# Revit family: Showerhead-American_Standard-FloWise-1660.613_Series
name_source: partatom
category: Plumbing Fixtures
units: mm (PartAtom-declared; Revit-internal decimal feet)

## family parameters
Always vertical = No
Cut with Voids When Loaded = No
OmniClass Number = 23.45.05.14.17
OmniClass Title = Showers
Part Type = Normal
Room Calculation Point = No
Round Connector Dimension = Use Diameter
Shared = Yes
Work Plane-Based = Yes

## types (1)
- 1660.613.002
    Assembly Code = D2010710
    CW Connection = No
    CWFU = 3
    Default Elevation = 0"
    Description = FloWise Modern 3-Function Water Saving Showerhead
    Finish = Brass-American Standard-002-Polished Chrome
    Flow Rate = 2.0 gpm Max Flow Rate
    HW Connection = No
    HWFU = 3
    Height = 4 3/4"
    Manufacturer = American Standard
    Material = Brass-American Standard-002-Polished Chrome
    Model = 1660.613.002
    Product Documentation Link = https://americanstandard.box.com
    Product URL = https://www.americanstandard-us.com
    Revised Date = 12/13/2011
    Tempered Connection Diameter = 1/2"
    Tempered Water Connection = Yes
    URL = http://www.americanstandard-us.com
    Vent Connection = No
    WFU = 4
    Waste Connection = No
    Width = 3 1/2"

## geometry (parser evidence)
native form markers: Sweep x3
no freeform markers — native parametric forms only
